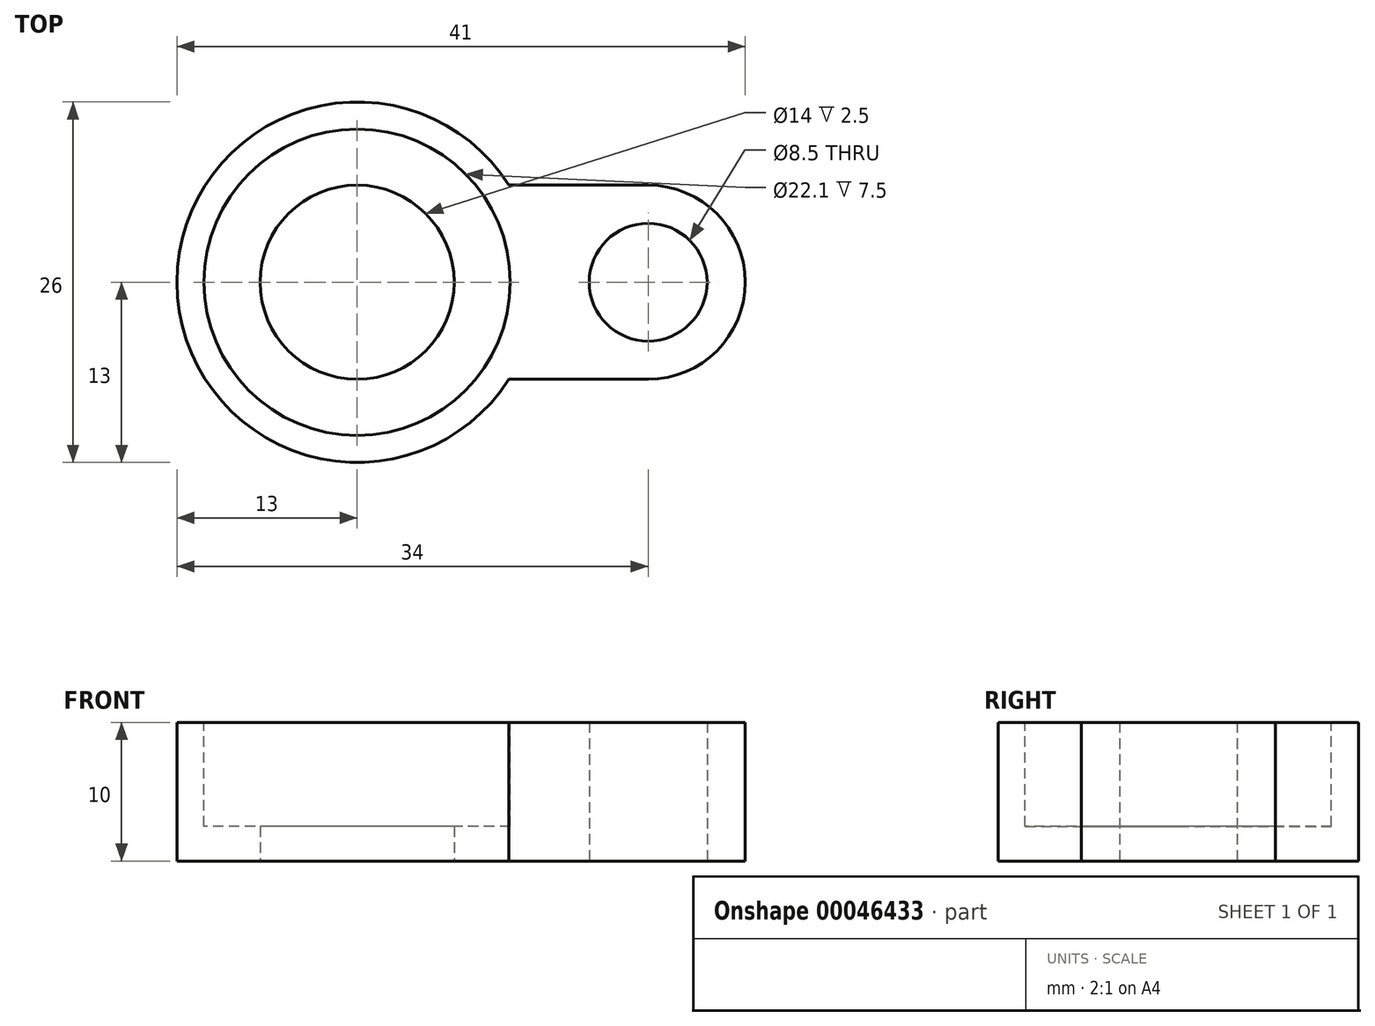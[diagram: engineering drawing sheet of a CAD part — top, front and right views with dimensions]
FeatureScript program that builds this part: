
annotation { "Feature Type Name" : "Feature", "Feature Type Description" : "" }
export const myFeature = defineFeature(function(context is Context, id is Id, definition is map)
    precondition{}
    {
        {
            var Q0;
            Q0=qCreatedBy(makeId("Top.planeOp"),FACE);
            var sketch = newSketch(context, id + "F0", { "sketchPlane" : qUnion([Q0])});
            skCircle(sketch, "E0", {"center": v(0, 0) * mm, "radius": 13 * mm});
            skPoint(sketch, "E1", {"position": v(21, 0) * mm});
            skCircle(sketch, "E2", {"center": v(21, 0) * mm, "radius": 4.25 * mm});
            skCircle(sketch, "E3", {"center": v(21, 0) * mm, "radius": 7 * mm});
            skLineSegment(sketch, "E4", {"start": v(21, 7) * mm, "end": v(10.95, 7) * mm});
            skLineSegment(sketch, "E5", {"start": v(21, -7) * mm, "end": v(10.95, -7) * mm});
            skCircle(sketch, "E6", {"center": v(0, 0) * mm, "radius": 7 * mm});
            skSolve(sketch);
        }
        {
            var Q0;
            Q0=makeQuery(id+"F0.imprint","IMPRINT",FACE,{"disambiguationData":[TD([[makeQuery(id+"F0.imprint","IMPRINT",EDGE,{"derivedFrom":sQuery(id+"F0.wireOp",EDGE,"E6")}),-1.0]])]});
            var Q1;
            {var subQ0=sQuery(id+"F0.wireOp",EDGE,"E4");Q1=makeQuery(id+"F0.imprint","IMPRINT",FACE,{"disambiguationData":[TD([[makeQuery(id+"F0.imprint","IMPRINT",EDGE,{"derivedFrom":subQ0}),1.0]])]});}
            var Q2;
            {var subQ0=sQuery(id+"F0.wireOp",EDGE,"E5");Q2=makeQuery(id+"F0.imprint","IMPRINT",FACE,{"disambiguationData":[TD([[makeQuery(id+"F0.imprint","IMPRINT",EDGE,{"derivedFrom":subQ0}),-1.0]])]});}
            var Q3;
            Q3=makeQuery(id+"F0.imprint","IMPRINT",FACE,{"disambiguationData":[TD([[makeQuery(id+"F0.imprint","IMPRINT",EDGE,{"derivedFrom":sQuery(id+"F0.wireOp",EDGE,"E2")}),-1.0]])]});
            extrude(context, id + "F1", {"entities" : qUnion([Q0, Q1, Q2, Q3]), "depth" : 10 * mm, "offsetDistance" : 25 * mm});
        }
        {
            var Q0;
            Q0=makeQuery(id+"F1.opExtrude","CAP_FACE",FACE,{"disambiguationData":[OSD([sQuery(id+"F0.wireOp",EDGE,"E0"),sQuery(id+"F0.wireOp",EDGE,"E2"),sQuery(id+"F0.wireOp",EDGE,"E3"),sQuery(id+"F0.wireOp",EDGE,"E4"),sQuery(id+"F0.wireOp",EDGE,"E5"),sQuery(id+"F0.wireOp",EDGE,"E6")])],"isStart":false});
            var sketch = newSketch(context, id + "F2", { "sketchPlane" : qUnion([Q0])});
            skCircle(sketch, "E7", {"center": v(0, 0) * mm, "radius": 11.05 * mm});
            skSolve(sketch);
        }
        {
            var Q0;
            Q0=makeQuery(id+"F2.imprint","IMPRINT",FACE,{"disambiguationData":[TD([[makeQuery(id+"F2.imprint","IMPRINT",EDGE,{"derivedFrom":sQuery(id+"F2.wireOp",EDGE,"E7")}),1.0]])]});
            extrude(context, id + "F3", {"entities" : qUnion([Q0]), "operationType" : NewBodyOperationType.REMOVE, "oppositeDirection" : true, "depth" : 7.5 * mm, "offsetDistance" : 25 * mm});
        }
    });
